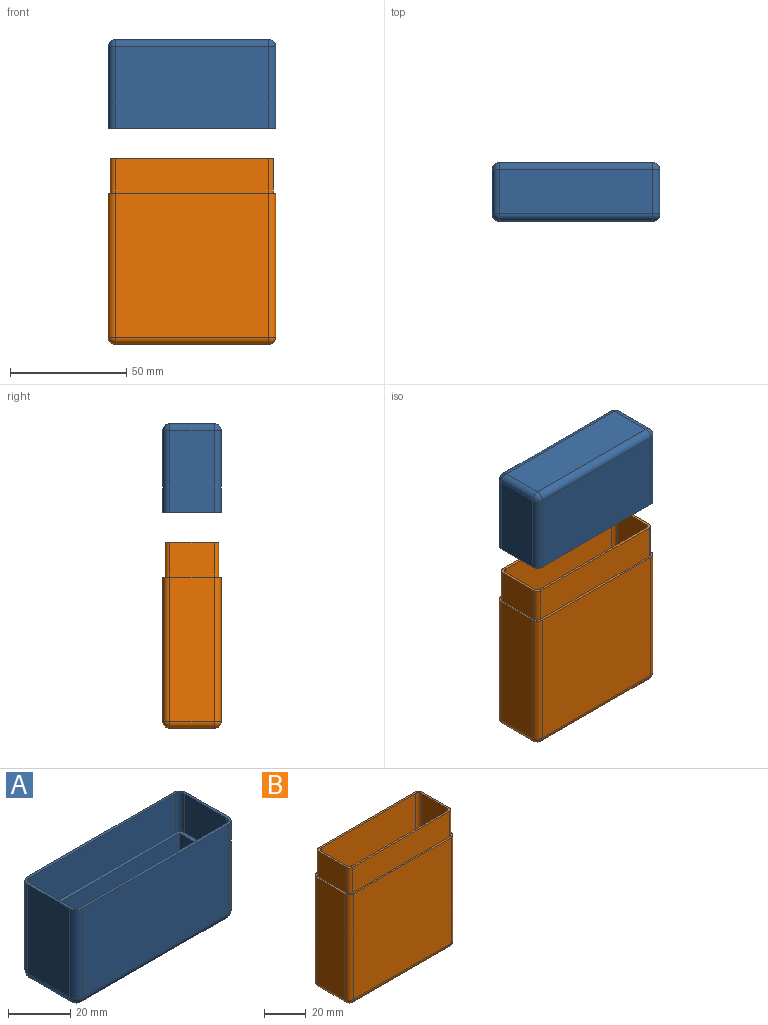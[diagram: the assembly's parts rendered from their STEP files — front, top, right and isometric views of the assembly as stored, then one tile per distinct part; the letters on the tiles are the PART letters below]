
ASSEMBLY  parts=2 mates=1
PART A: 32 faces, bbox 72x25x38 mm
  f0: plane 72x25mm, normal (0,0,1), area 161.5mm2, adj f1,f2,f3,f4,f6,f7,f8,f9
  f1: plane 35x19mm, normal (-1,0,0), area 665mm2, adj f0,f25,f29,f31
  f2: plane 66x35mm, normal (0,-1,0), area 2310mm2, adj f0,f22,f28,f31
  f3: plane 35x19mm, normal (1,0,0), area 665mm2, adj f0,f20,f22,f23
  f4: plane 66x35mm, normal (0,1,0), area 2310mm2, adj f0,f20,f24,f25
  f5: plane 66x19mm, normal (0,0,-1), area 1254mm2, adj f23,f24,f28,f29
  f6: plane 66.26x15.4mm, normal (0,-1,0), area 1020.4mm2, adj f0,f10,f16,f19
  f7: plane 19.26x15.4mm, normal (1,0,0), area 296.6mm2, adj f0,f10,f16,f17
  f8: plane 66.26x15.4mm, normal (0,1,0), area 1020.4mm2, adj f0,f10,f17,f18
  f9: plane 19.26x15.4mm, normal (-1,0,0), area 296.6mm2, adj f0,f10,f18,f19
  f10: plane 70.26x23.26mm, normal (0,0,1), area 202.8mm2, adj f6,f7,f8,f9,f12,f13,f14,f15
  f11: plane 68x21mm, normal (0,0,1), area 1428mm2, adj f12,f13,f14,f15
  f12: plane 68x20.6mm, normal (0,-1,0), area 1400.8mm2, adj f10,f11,f13,f15
  f13: plane 21x20.6mm, normal (-1,0,0), area 432.6mm2, adj f10,f11,f12,f14
  f14: plane 68x20.6mm, normal (0,1,0), area 1400.8mm2, adj f10,f11,f13,f15
  f15: plane 21x20.6mm, normal (1,0,0), area 432.6mm2, adj f10,f11,f12,f14
  f16: cylinder r=2mm len=15.4mm, axis (0,0,-1), area 48.4mm2, adj f0,f6,f7,f10
  f17: cylinder r=2mm len=15.4mm, axis (0,0,1), area 48.4mm2, adj f0,f7,f8,f10
  f18: cylinder r=2mm len=15.4mm, axis (0,0,-1), area 48.4mm2, adj f0,f8,f9,f10
  f19: cylinder r=2mm len=15.4mm, axis (0,0,1), area 48.4mm2, adj f0,f6,f9,f10
  f20: cylinder r=3mm len=35mm, axis (0,0,1), area 164.9mm2, adj f0,f3,f4,f21
  f21: sphere r=3mm, area 14.1mm2, adj f20,f23,f24
  f22: cylinder r=3mm len=35mm, axis (0,0,-1), area 164.9mm2, adj f0,f2,f3,f26
  f23: cylinder r=3mm len=19mm, axis (0,1,0), area 89.5mm2, adj f3,f5,f21,f26
  f24: cylinder r=3mm len=66mm, axis (-1,0,0), area 311mm2, adj f4,f5,f21,f27
  f25: cylinder r=3mm len=35mm, axis (0,0,-1), area 164.9mm2, adj f0,f1,f4,f27
  f26: sphere r=3mm, area 14.1mm2, adj f22,f23,f28
  f27: sphere r=3mm, area 14.1mm2, adj f24,f25,f29
  f28: cylinder r=3mm len=66mm, axis (1,0,0), area 311mm2, adj f2,f5,f26,f30
  f29: cylinder r=3mm len=19mm, axis (0,-1,0), area 89.5mm2, adj f1,f5,f27,f30
  f30: sphere r=3mm, area 14.1mm2, adj f28,f29,f31
  f31: cylinder r=3mm len=35mm, axis (0,0,1), area 164.9mm2, adj f0,f1,f2,f30
PART B: 36 faces, bbox 72x25x80 mm
  f0: plane 70.04x23.04mm, normal (0,0,1), area 185.7mm2, adj f1,f3,f4,f5,f6,f7,f8,f9
  f1: plane 78x17mm, normal (1,0,0), area 1326mm2, adj f0,f2,f32,f34
  f2: plane 68x21mm, normal (0,0,1), area 1424.6mm2, adj f1,f3,f4,f5,f32,f33,f34,f35
  f3: plane 78x17mm, normal (-1,0,0), area 1326mm2, adj f0,f2,f33,f35
  f4: plane 78x64mm, normal (0,1,0), area 4992mm2, adj f0,f2,f32,f35
  f5: plane 78x64mm, normal (0,-1,0), area 4992mm2, adj f0,f2,f33,f34
  f6: plane 19.04x15mm, normal (-1,0,0), area 285.6mm2, adj f0,f10,f28,f31
  f7: plane 66.04x15mm, normal (0,1,0), area 990.6mm2, adj f0,f10,f28,f29
  f8: plane 19.04x15mm, normal (1,0,0), area 285.6mm2, adj f0,f10,f29,f30
  f9: plane 66.04x15mm, normal (0,-1,0), area 990.6mm2, adj f0,f10,f30,f31
  f10: plane 72x25mm, normal (0,0,1), area 182mm2, adj f6,f7,f8,f9,f12,f13,f14,f15
  f11: plane 66x19mm, normal (0,0,-1), area 1254mm2, adj f17,f22,f23,f27
  f12: plane 66x62mm, normal (0,1,0), area 4092mm2, adj f10,f18,f23,f24
  f13: plane 66x62mm, normal (0,-1,0), area 4092mm2, adj f10,f16,f21,f22
  f14: plane 62x19mm, normal (1,0,0), area 1178mm2, adj f10,f16,f17,f18
  f15: plane 62x19mm, normal (-1,0,0), area 1178mm2, adj f10,f21,f24,f27
  f16: cylinder r=3mm len=62mm, axis (0,0,-1), area 292.2mm2, adj f10,f13,f14,f19
  f17: cylinder r=3mm len=19mm, axis (0,1,0), area 89.5mm2, adj f11,f14,f19,f20
  f18: cylinder r=3mm len=62mm, axis (0,0,1), area 292.2mm2, adj f10,f12,f14,f20
  f19: sphere r=3mm, area 14.1mm2, adj f16,f17,f22
  f20: sphere r=3mm, area 14.1mm2, adj f17,f18,f23
  f21: cylinder r=3mm len=62mm, axis (0,0,1), area 292.2mm2, adj f10,f13,f15,f25
  f22: cylinder r=3mm len=66mm, axis (-1,0,0), area 311mm2, adj f11,f13,f19,f25
  f23: cylinder r=3mm len=66mm, axis (1,0,0), area 311mm2, adj f11,f12,f20,f26
  f24: cylinder r=3mm len=62mm, axis (0,0,-1), area 292.2mm2, adj f10,f12,f15,f26
  f25: sphere r=3mm, area 14.1mm2, adj f21,f22,f27
  f26: sphere r=3mm, area 14.1mm2, adj f23,f24,f27
  f27: cylinder r=3mm len=19mm, axis (0,-1,0), area 89.5mm2, adj f11,f15,f25,f26
  f28: cylinder r=2mm len=15mm, axis (0,0,1), area 47.1mm2, adj f0,f6,f7,f10
  f29: cylinder r=2mm len=15mm, axis (0,0,-1), area 47.1mm2, adj f0,f7,f8,f10
  f30: cylinder r=2mm len=15mm, axis (0,0,1), area 47.1mm2, adj f0,f8,f9,f10
  f31: cylinder r=2mm len=15mm, axis (0,0,-1), area 47.1mm2, adj f0,f6,f9,f10
  f32: cylinder r=2mm len=78mm, axis (0,0,-1), area 245mm2, adj f0,f1,f2,f4
  f33: cylinder r=2mm len=78mm, axis (0,0,-1), area 245mm2, adj f0,f2,f3,f5
  f34: cylinder r=2mm len=78mm, axis (0,0,1), area 245mm2, adj f0,f1,f2,f5
  f35: cylinder r=2mm len=78mm, axis (0,0,1), area 245mm2, adj f0,f2,f3,f4
PLACE A rot(axis=(0,-1,0),180deg) t=(-47.84,-16.59,109.41)mm
PLACE B rot(axis=(0.22,0.75,0.63),0deg) t=(-47.95,-4.09,18.5)mm
MATE slider A.f0 <-> B.f0  axis (0,0,-1) through (-82.97,-16.59,71.41)mm
